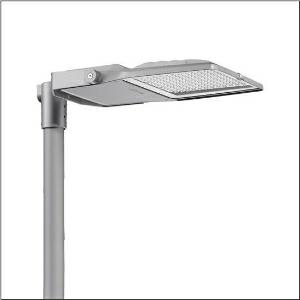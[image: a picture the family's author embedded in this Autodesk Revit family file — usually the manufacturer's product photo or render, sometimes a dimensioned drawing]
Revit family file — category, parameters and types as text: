
# Revit family: floodlight_fl_21_iq_midi___pl43_5xa7782e4a3a_f2c8
name_source: partatom
category: Lighting Fixtures
units: mm (PartAtom-declared; Revit-internal decimal feet)

## family parameters
Cut with Voids When Loaded = No
Host = Face
Light Source = No
Part Type = Normal
Room Calculation Point = No
Round Connector Dimension = Use Diameter
Shared = No

## types (1)
- --- (1 x LED, 28730 lm, 208.1 W, 4000K)
    Apparent Load = 208 VA
    CIE Flux Codes = 27 78 99 100 100
    Color Rendering = 70
    Color Temperature = 4000K
    Default Elevation = 1800 mm
    Description = Floodlight FL 21 iQ midi, floodlight, primary light control with lens, of PMMA, primary optical cover: protective disc, of toughened safety glass, transparent, light distribution: PL43, light emission: direct distribution, installation type: surface-mounted, lamps: LED, High Power LED, rated values: 28.730lm | 208,1W | 138,1lm/W (begin service life); end service life: 28.730lm | 227,1W; at 50% lumin. flux: 14.365lm | 90,3W | 159,1lm/W, colour temperature: 4000K, colour rendering: CRI > 70, light colour: 740, light setting 1 begin service life: 100% | 28.730lm | 208,1W | 138,1lm/W | 4.000K, light setting 1 end service life: 227,1W, further light settings possible, control: optimised constant luminous flux control (CLO 2.0), Desk-Remote (wireless, voltage-free reading and setting of iQ features in the workshop via application-optimized NFC function/RFID function), Smart-Wire, Night-Set, Temp-Guard, Auto-Match, Street-Remote, pre-setting: linear dimming characteristic, with terminal, 6-pole, mains connection: 220..240V, AC, 50/60Hz, luminaire housing, of diecast aluminium, powder-coated, SITECO metallic grey (DB 702S), corrosivity category C5 mid according to DIN EN ISO 12944suitable for swimming poolschlorine-resistant, sealing non-destructively replaceable, please order mast flange separately, mast bracket, of steel, galvanised, powder-coated, SITECO metallic grey (DB 702S), protection rating (complete): IP66, insulation class (complete): insulation class II (safety insulation), certification: CE, ENEC, VDE, protection symbol: D, impact resistance: IK08, permissible operating ambient temperature: -40..+40°C, permissible operating ambient temperature for outdoor applications: -40..+50°C, standard: DIN EN 12944, LABS conformity tested according to VDMA 24364:2018-05, packaging unit: 1 piece

Light Distribution: PL43
    Height = 76 mm
    Lamp = 1 x LED
    Lamp Light Flux = 28730 lm
    Lamp Power = 208.1 W
    Lamp count = 1
    Length = 657 mm
    Luminous efficacy = 138 lm/W
    Manufacturer = Siteco
    ModVariant = No
    Model = 5XA7782E4A3A
    Number of Poles = 1
    OnlyDefault = Yes
    Power Factor = 1
    Product Name = Floodlight FL 21 iQ midi | PL43
    Product group = floodlight | pylon annexe
    ProductGroupID = 6201
    Protection Class = Protection class II
    Protection Degree = IP 66
    RLX_Detail_Level = 1
    RLX_Emergency_Light_Flux = 0 lm
    RLX_Emergency_Type = 0
    RLX_Emergency_Type_DB = No
    RlxData = <blob elided: 153681 chars, md5=11c15e7f>
    Socket = socket
    Standby Power = 0 W
    System Light Flux = 28730 lm
    System Power = 208 W
    Type Comments = factory setting: luminous flux: 100 % | dim-lin: 254 | 710 mA
    Type Image = l_1007123.jpg
    URL = http://relux.com
    VarID = @adj_105017
    Voltage = 0 V
    Weight = 0.00 kg
    Width = 442 mm

## geometry (parser evidence)
native form markers: Blend x4, Sweep x14
no freeform markers — native parametric forms only
